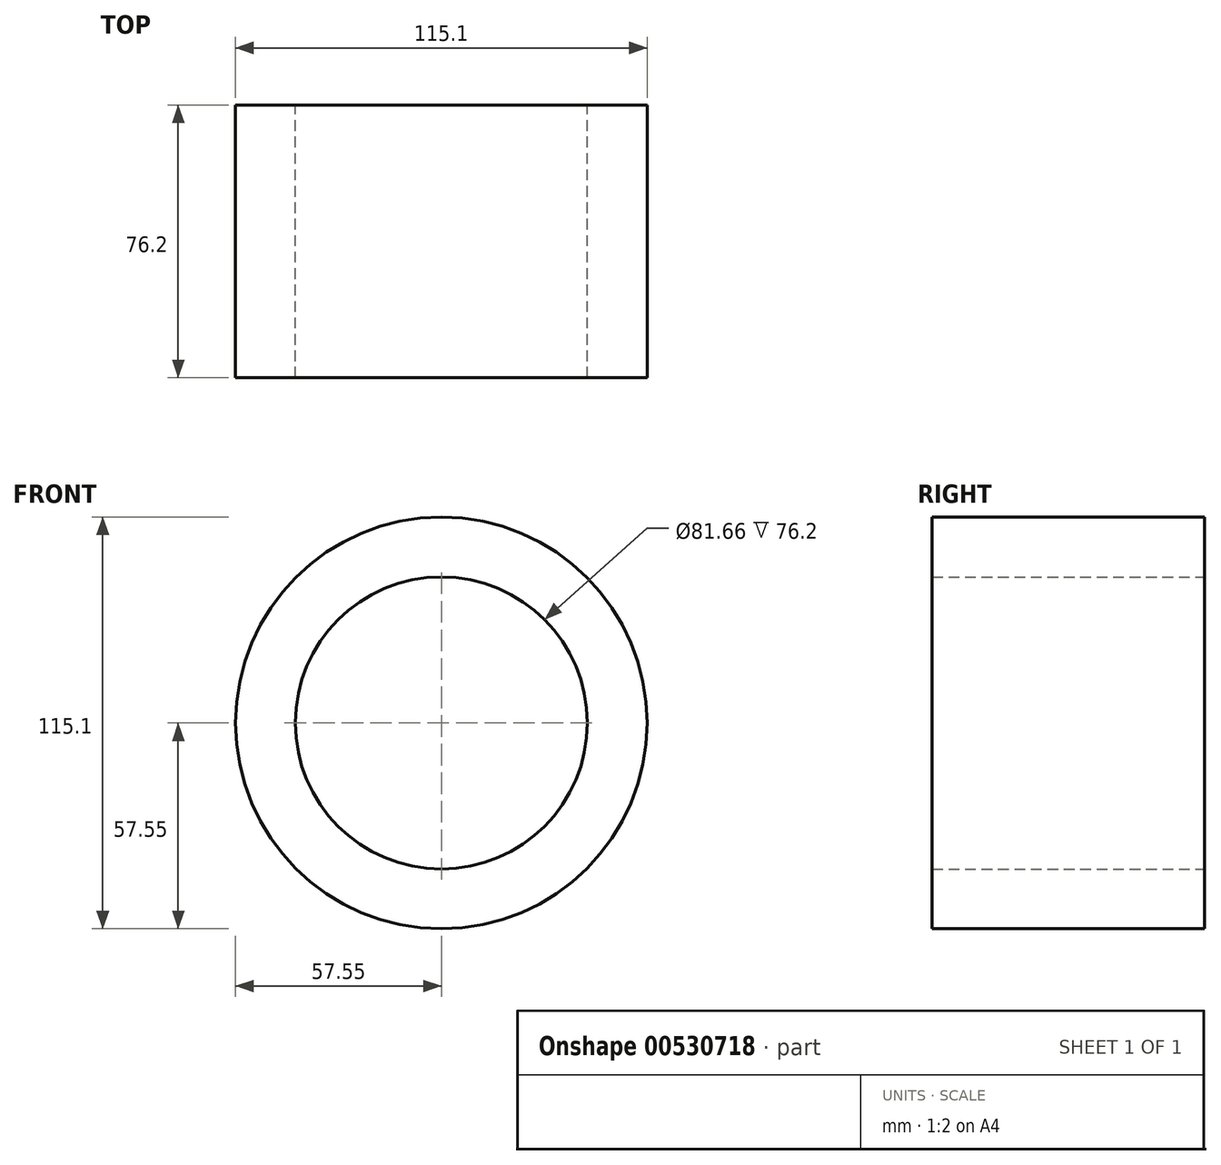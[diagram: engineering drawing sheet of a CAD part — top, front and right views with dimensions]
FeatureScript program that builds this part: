
annotation { "Feature Type Name" : "Feature", "Feature Type Description" : "" }
export const myFeature = defineFeature(function(context is Context, id is Id, definition is map)
    precondition{}
    {
        {
            var Q0;
            Q0=qCreatedBy(makeId("Front.planeOp"),FACE);
            var sketch = newSketch(context, id + "F0", { "sketchPlane" : qUnion([Q0])});
            skCircle(sketch, "E0", {"center": v(0, 0) * mm, "radius": 57.55 * mm});
            skCircle(sketch, "E1", {"center": v(0, 0) * mm, "radius": 40.83 * mm});
            skSolve(sketch);
        }
        {
            var Q0;
            Q0 = qSketchRegion(id + "F0", true);
            extrude(context, id + "F1", {"entities" : qUnion([Q0]), "depth" : 76.2 * mm, "offsetDistance" : 25.4 * mm});
        }
    });
